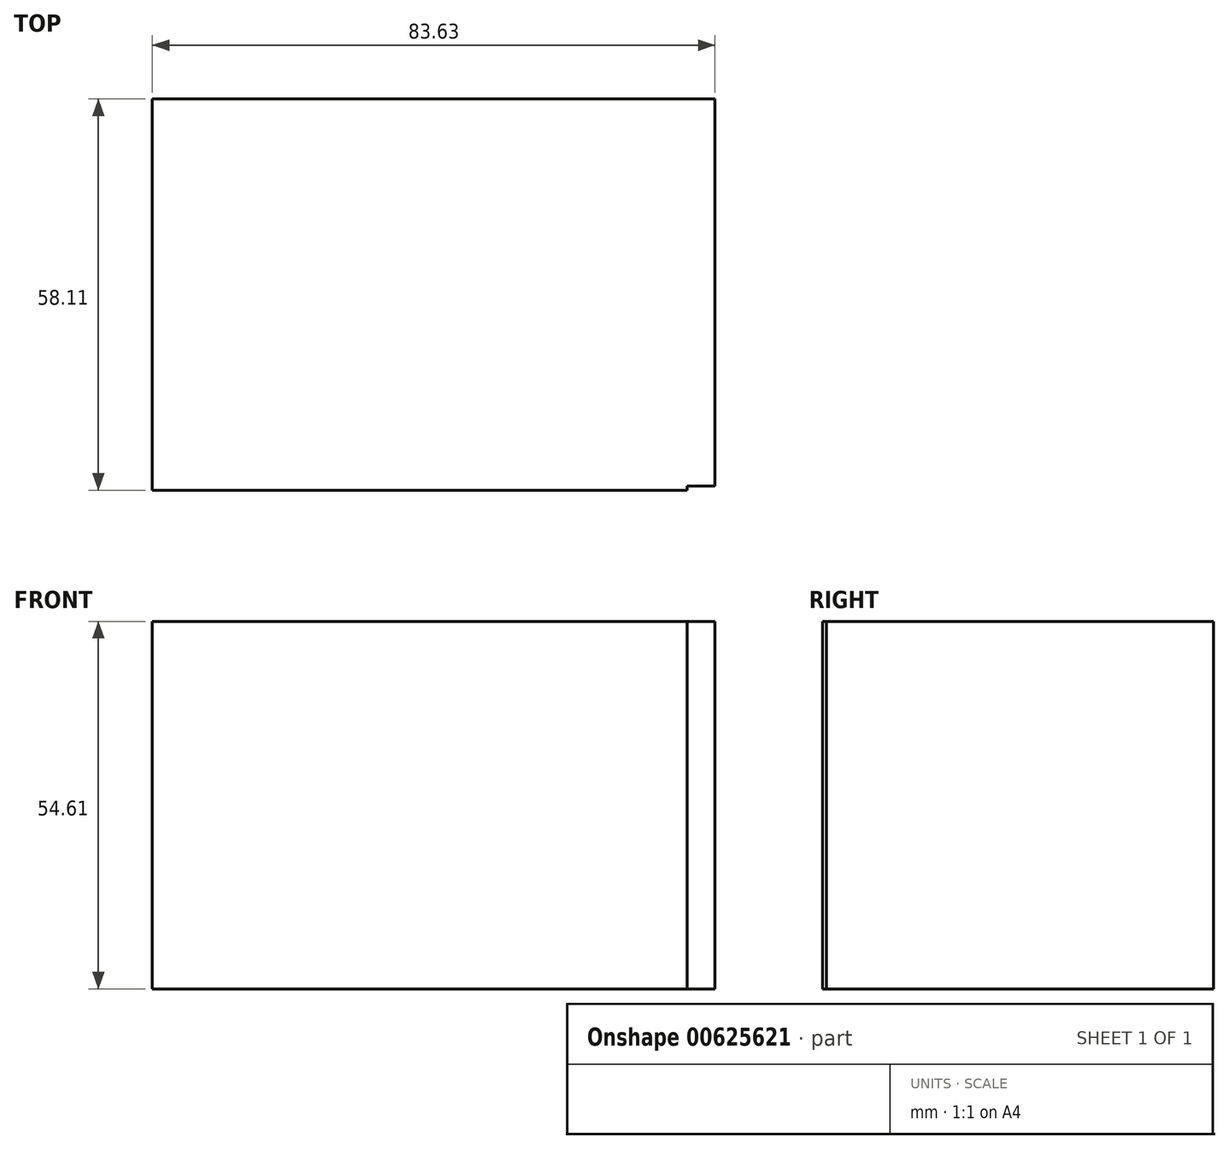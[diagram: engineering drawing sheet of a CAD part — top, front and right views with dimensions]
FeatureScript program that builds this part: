
annotation { "Feature Type Name" : "Feature", "Feature Type Description" : "" }
export const myFeature = defineFeature(function(context is Context, id is Id, definition is map)
    precondition{}
    {
        {
            var Q0;
            Q0=qCreatedBy(makeId("Top.planeOp"),FACE);
            var sketch = newSketch(context, id + "F0", { "sketchPlane" : qUnion([Q0])});
            skLineSegment(sketch, "E0.bottom", {"start": v(-83.63, 42.43) * mm, "end": v(0, 42.43) * mm});
            skLineSegment(sketch, "E0.top", {"start": v(-83.63, -15.68) * mm, "end": v(0, -15.68) * mm});
            skLineSegment(sketch, "E0.left", {"start": v(-83.63, 42.43) * mm, "end": v(-83.63, -15.68) * mm});
            skLineSegment(sketch, "E0.right", {"start": v(0, 42.43) * mm, "end": v(0, -15.68) * mm});
            skLineSegment(sketch, "E1.bottom", {"start": v(-4.17, -15.1) * mm, "end": v(0, -15.1) * mm});
            skLineSegment(sketch, "E1.top", {"start": v(-4.17, -15.68) * mm, "end": v(0, -15.68) * mm});
            skLineSegment(sketch, "E1.left", {"start": v(-4.17, -15.1) * mm, "end": v(-4.17, -15.68) * mm});
            skLineSegment(sketch, "E1.right", {"start": v(0, -15.1) * mm, "end": v(0, -15.68) * mm});
            skSolve(sketch);
        }
        {
            var Q0;
            Q0=makeQuery(id+"F0.imprint","IMPRINT",FACE,{"disambiguationData":[TD([[makeQuery(id+"F0.imprint","IMPRINT",EDGE,{"derivedFrom":sQuery(id+"F0.wireOp",EDGE,"E0.bottom")}),-1.0]])]});
            extrude(context, id + "F1", {"entities" : qUnion([Q0]), "depth" : 54.6 * mm, "offsetDistance" : 25.4 * mm});
        }
    });
